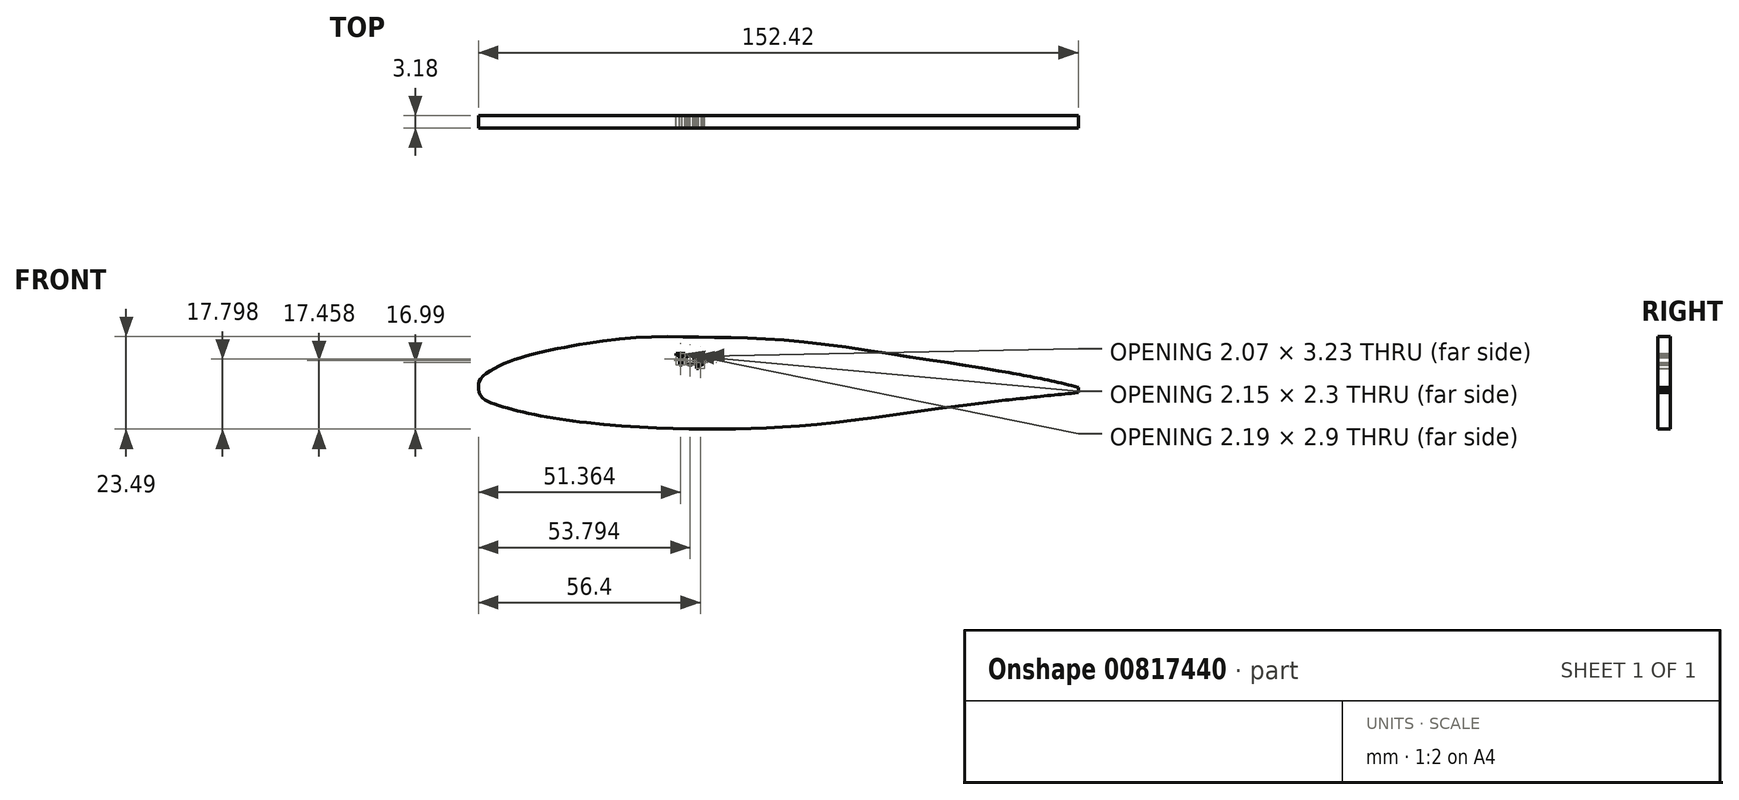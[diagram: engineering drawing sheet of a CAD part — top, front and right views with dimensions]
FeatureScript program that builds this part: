
annotation { "Feature Type Name" : "Feature", "Feature Type Description" : "" }
export const myFeature = defineFeature(function(context is Context, id is Id, definition is map)
    precondition{}
    {
        {
            var Q0;
            Q0=qCreatedBy(makeId("Front.planeOp"),FACE);
            var sketch = newSketch(context, id + "F0", { "sketchPlane" : qUnion([Q0])});
            skLineSegment(sketch, "E0", {"start": v(82.65, 0) * mm, "end": v(-69.75, 0) * mm});
            skFitSpline(sketch, "E1", {"points": [v(82.65, 0.37) * mm, v(65.26, 4.07) * mm, v(42.83, 7.66) * mm, v(9.87, 12.2) * mm, v(-12.79, 13.13) * mm, v(-31.29, 12.9) * mm, v(-50.97, 9.94) * mm, v(-63.44, 6.28) * mm, v(-69.45, 2.2) * mm, v(-69.75, 0) * mm], "startDerivative": vector(-144.04, 37.3) * mm, "endDerivative": vector(1, -51.16) * mm});
            skFitSpline(sketch, "E2", {"points": [v(82.65, -0.96) * mm, v(53.63, -4.17) * mm, v(18.72, -8.81) * mm, v(-3.74, -10.18) * mm, v(-24.44, -9.94) * mm, v(-49.64, -7.64) * mm, v(-65.73, -3.87) * mm, v(-69.75, 0) * mm], "startDerivative": vector(-165.49, -16.43) * mm, "endDerivative": vector(-11.78, 96.6) * mm});
            skLineSegment(sketch, "E3", {"start": v(62.32, 11.37) * mm, "end": v(62.32, -13.84) * mm});
            skLineSegment(sketch, "E4", {"start": v(-42.35, 15.77) * mm, "end": v(-42.35, -15.08) * mm});
            skText(sketch, "E5", { "text": "Top\n", "fontName": "OpenSans-Bold.ttf"});
            skLineSegment(sketch, "E6", {"start": v(82.65, -0.93) * mm, "end": v(82.65, 0.4) * mm});
            skLineSegment(sketch, "E7", {"start": v(82.65, 0.37) * mm, "end": v(82.65, -0.96) * mm});
            skPoint(sketch, "E8", {"position": v(82.65, -0.93) * mm});
            skPoint(sketch, "E9", {"position": v(82.65, 0.4) * mm});
            skPoint(sketch, "E10", {"position": v(82.65, 0) * mm});
            const initialGuessF0  = {"E5": [-0.01958, 0.0061, 1, 0, 0.00292]};
            skSetInitialGuess(sketch, initialGuessF0);
            skSolve(sketch);
        }
        {
            var Q0;
            {var subQ0=sQuery(id+"F0.wireOp",EDGE,"E3");var subQ1=sQuery(id+"F0.wireOp",EDGE,"E0");var subQ2=makeQuery(id+"F0.imprint","INTERSECT",VERTEX,{"derivedFrom":[subQ1,subQ0]});Q0=makeQuery(id+"F0.imprint","IMPRINT",FACE,{"disambiguationData":[TD([[makeQuery(id+"F0.imprint","IMPRINT",EDGE,{"disambiguationData":[TD([[subQ2,-1.0]])],"derivedFrom":subQ1}),1.0]])]});}
            var Q1;
            {var subQ0=sQuery(id+"F0.wireOp",EDGE,"E2");var subQ3=sQuery(id+"F0.wireOp",EDGE,"E4");var subQ5=makeQuery(id+"F0.imprint","INTERSECT",VERTEX,{"derivedFrom":[subQ0,subQ3]});Q1=makeQuery(id+"F0.imprint","IMPRINT",FACE,{"disambiguationData":[TD([[makeQuery(id+"F0.imprint","IMPRINT",EDGE,{"disambiguationData":[TD([[subQ5,1.0]])],"derivedFrom":subQ3}),-1.0]])]});}
            var Q2;
            Q2=makeQuery(id+"F0.imprint","IMPRINT",FACE,{"disambiguationData":[TD([[makeQuery(id+"F0.imprint","IMPRINT",EDGE,{"derivedFrom":sQuery(id+"F0.wireOp",EDGE,"E5.sketch_text.stroke-0")}),1.0]])]});
            var Q3;
            {var subQ0=sQuery(id+"F0.wireOp",EDGE,"E1");var subQ3=sQuery(id+"F0.wireOp",EDGE,"E4");var subQ5=makeQuery(id+"F0.imprint","INTERSECT",VERTEX,{"derivedFrom":[subQ0,subQ3]});Q3=makeQuery(id+"F0.imprint","IMPRINT",FACE,{"disambiguationData":[TD([[makeQuery(id+"F0.imprint","IMPRINT",EDGE,{"disambiguationData":[TD([[subQ5,-1.0]])],"derivedFrom":subQ3}),-1.0]])]});}
            var Q4;
            {var subQ0=sQuery(id+"F0.wireOp",EDGE,"E6");var subQ1=sQuery(id+"F0.wireOp",EDGE,"E0");var subQ2=makeQuery(id+"F0.imprint","INTERSECT",VERTEX,{"derivedFrom":[subQ1,subQ0]});Q4=makeQuery(id+"F0.imprint","IMPRINT",FACE,{"disambiguationData":[TD([[makeQuery(id+"F0.imprint","IMPRINT",EDGE,{"disambiguationData":[TD([[subQ2,-1.0]])],"derivedFrom":subQ1}),-1.0]])]});}
            var Q5;
            {var subQ0=sQuery(id+"F0.wireOp",EDGE,"E6");var subQ1=sQuery(id+"F0.wireOp",EDGE,"E0");var subQ2=makeQuery(id+"F0.imprint","INTERSECT",VERTEX,{"derivedFrom":[subQ1,subQ0]});Q5=makeQuery(id+"F0.imprint","IMPRINT",FACE,{"disambiguationData":[TD([[makeQuery(id+"F0.imprint","IMPRINT",EDGE,{"disambiguationData":[TD([[subQ2,-1.0]])],"derivedFrom":subQ1}),1.0]])]});}
            extrude(context, id + "F1", {"entities" : qUnion([Q0, Q1, Q2, Q3, Q4, Q5]), "depth" : 3.17 * mm, "offsetDistance" : 25.4 * mm});
        }
    });
